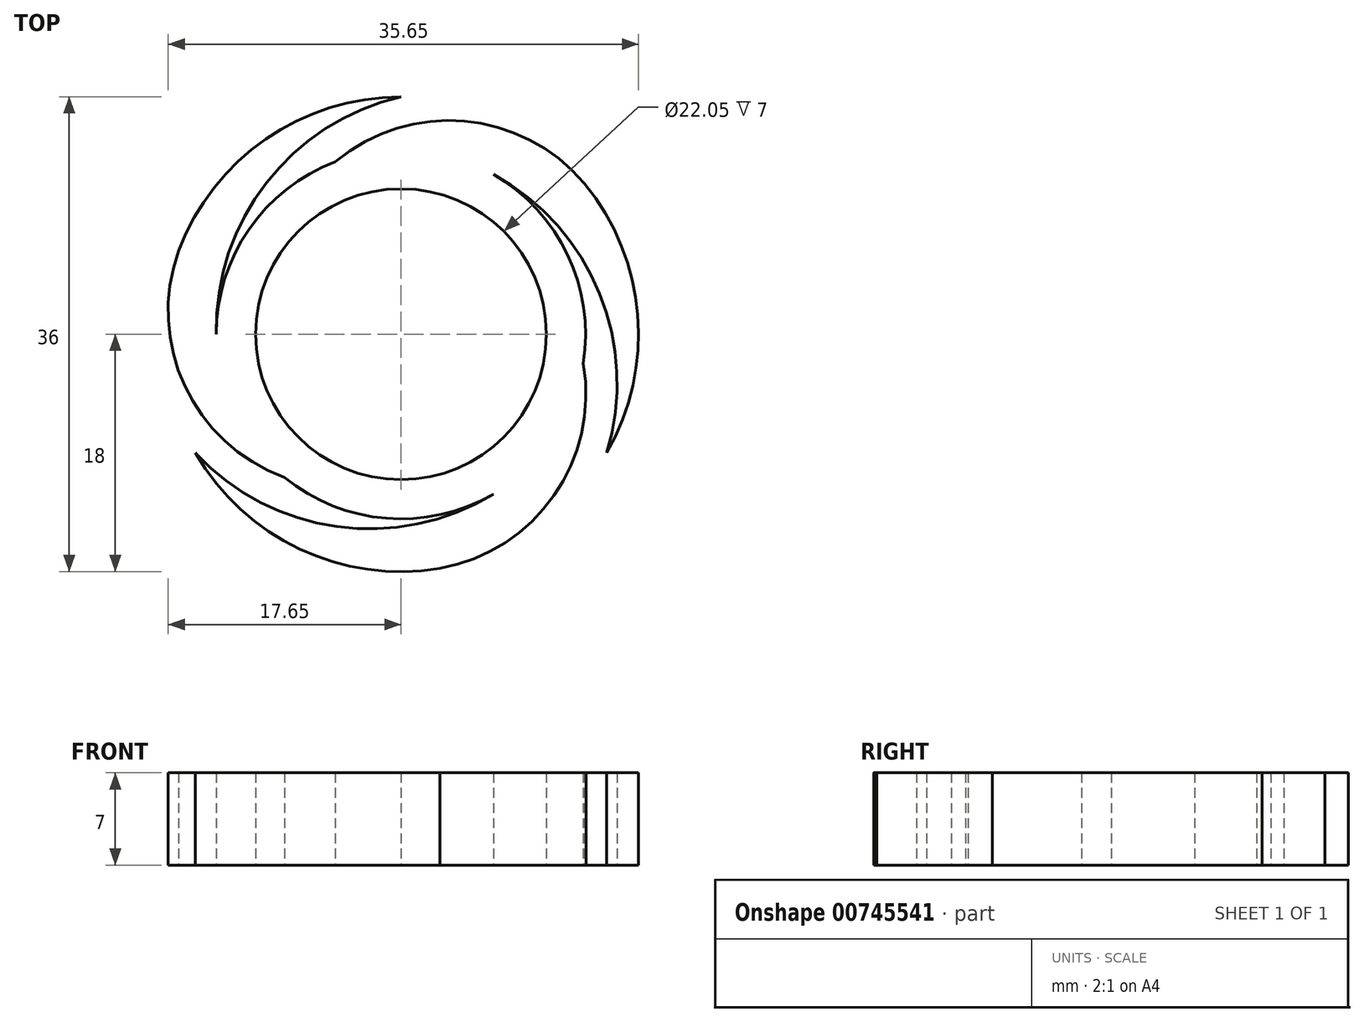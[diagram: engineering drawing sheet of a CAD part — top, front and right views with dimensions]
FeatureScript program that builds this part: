
annotation { "Feature Type Name" : "Feature", "Feature Type Description" : "" }
export const myFeature = defineFeature(function(context is Context, id is Id, definition is map)
    precondition{}
    {
        {
            var Q0;
            Q0=qCreatedBy(makeId("Top.planeOp"),FACE);
            var sketch = newSketch(context, id + "F0", { "sketchPlane" : qUnion([Q0])});
            skCircle(sketch, "E0", {"center": v(0, 0) * mm, "radius": 11.03 * mm});
            skCircle(sketch, "E1", {"center": v(0, 0) * mm, "radius": 14 * mm});
            skArc(sketch, "E2", {"start": v(0, 18) * mm, "mid": v(-10.25, 14.8) * mm, "end": v(-16.85, 6.32) * mm});
            skArc(sketch, "E3", {"start": v(0, 18) * mm, "mid": v(-10.2, 11.5) * mm, "end": v(-14, 0) * mm});
            skArc(sketch, "E4.1.0", {"start": v(-15.59, -9) * mm, "mid": v(-4.85, -14.58) * mm, "end": v(7, -12.12) * mm});
            skArc(sketch, "E4.2.0", {"start": v(15.59, -9) * mm, "mid": v(15.05, 3.1) * mm, "end": v(7, 12.12) * mm});
            skArc(sketch, "E5", {"start": v(-16.35, 7.52) * mm, "mid": v(-16.65, -3.32) * mm, "end": v(-8.84, -10.85) * mm});
            skArc(sketch, "E6.1.0", {"start": v(1.67, -17.92) * mm, "mid": v(11.2, -12.76) * mm, "end": v(13.82, -2.23) * mm});
            skArc(sketch, "E6.2.0", {"start": v(14.69, 10.4) * mm, "mid": v(5.45, 16.08) * mm, "end": v(-4.98, 13.09) * mm});
            skArc(sketch, "E7.trimOffspring", {"start": v(15.59, -9) * mm, "mid": v(17.94, 1.48) * mm, "end": v(13.9, 11.43) * mm});
            skArc(sketch, "E8.trimOffspring", {"start": v(-15.59, -9) * mm, "mid": v(-7.69, -16.28) * mm, "end": v(2.95, -17.76) * mm});
            skSolve(sketch);
        }
        {
            var Q0;
            Q0=makeQuery(id+"F0.imprint","IMPRINT",FACE,{"disambiguationData":[TD([[makeQuery(id+"F0.imprint","IMPRINT",EDGE,{"derivedFrom":sQuery(id+"F0.wireOp",EDGE,"E0")}),-1.0]])]});
            var Q1;
            {var subQ0=sQuery(id+"F0.wireOp",EDGE,"E3");Q1=makeQuery(id+"F0.imprint","IMPRINT",FACE,{"disambiguationData":[TD([[makeQuery(id+"F0.imprint","IMPRINT",EDGE,{"derivedFrom":subQ0}),-1.0]])]});}
            var Q2;
            {var subQ1=sQuery(id+"F0.wireOp",EDGE,"E4.2.0");Q2=makeQuery(id+"F0.imprint","IMPRINT",FACE,{"disambiguationData":[TD([[makeQuery(id+"F0.imprint","IMPRINT",EDGE,{"derivedFrom":subQ1}),-1.0]])]});}
            var Q3;
            {var subQ1=sQuery(id+"F0.wireOp",EDGE,"E4.1.0");Q3=makeQuery(id+"F0.imprint","IMPRINT",FACE,{"disambiguationData":[TD([[makeQuery(id+"F0.imprint","IMPRINT",EDGE,{"derivedFrom":subQ1}),-1.0]])]});}
            extrude(context, id + "F1", {"entities" : qUnion([Q0, Q1, Q2, Q3]), "depth" : 7 * mm, "offsetDistance" : 25.4 * mm});
        }
    });
